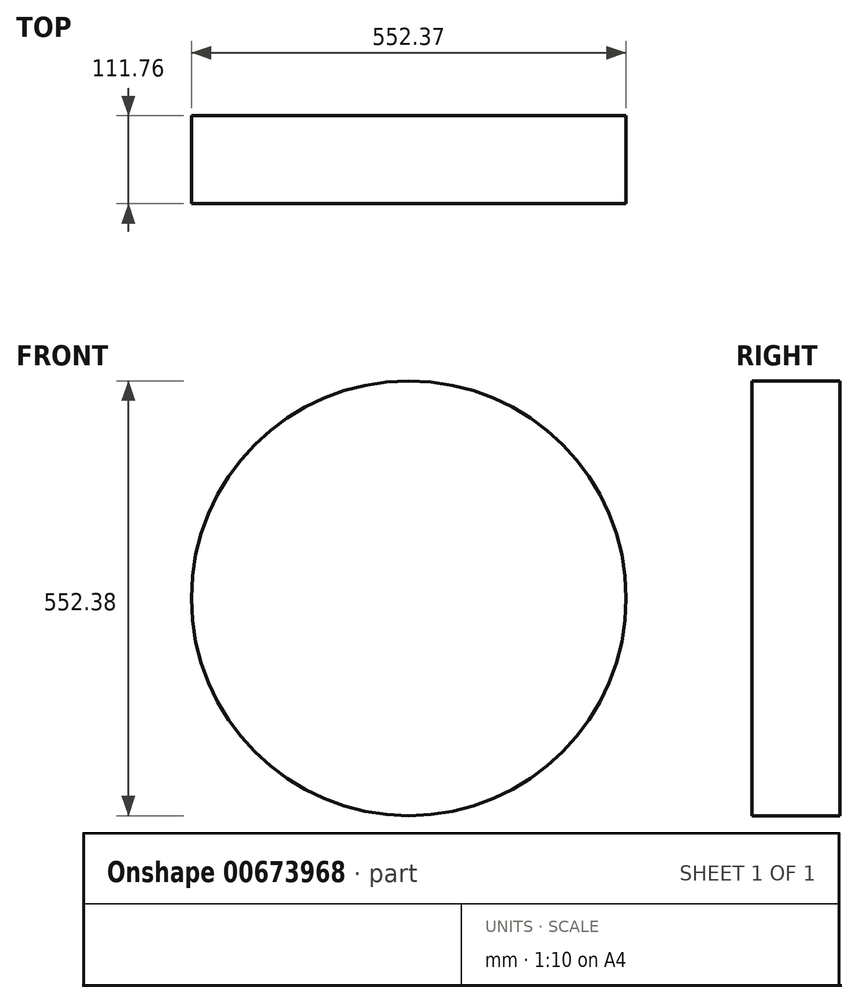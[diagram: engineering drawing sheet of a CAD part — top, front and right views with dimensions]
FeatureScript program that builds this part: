
annotation { "Feature Type Name" : "Feature", "Feature Type Description" : "" }
export const myFeature = defineFeature(function(context is Context, id is Id, definition is map)
    precondition{}
    {
        {
            var Q0;
            Q0=qCreatedBy(makeId("Front.planeOp"),FACE);
            var sketch = newSketch(context, id + "F0", { "sketchPlane" : qUnion([Q0])});
            skCircle(sketch, "E0", {"center": v(-276.19, 10.87) * mm, "radius": 276.19 * mm});
            skSolve(sketch);
        }
        {
            var Q0;
            Q0 = qSketchRegion(id + "F0", true);
            extrude(context, id + "F1", {"entities" : qUnion([Q0]), "depth" : 111.76 * mm, "offsetDistance" : 25.4 * mm});
        }
    });
